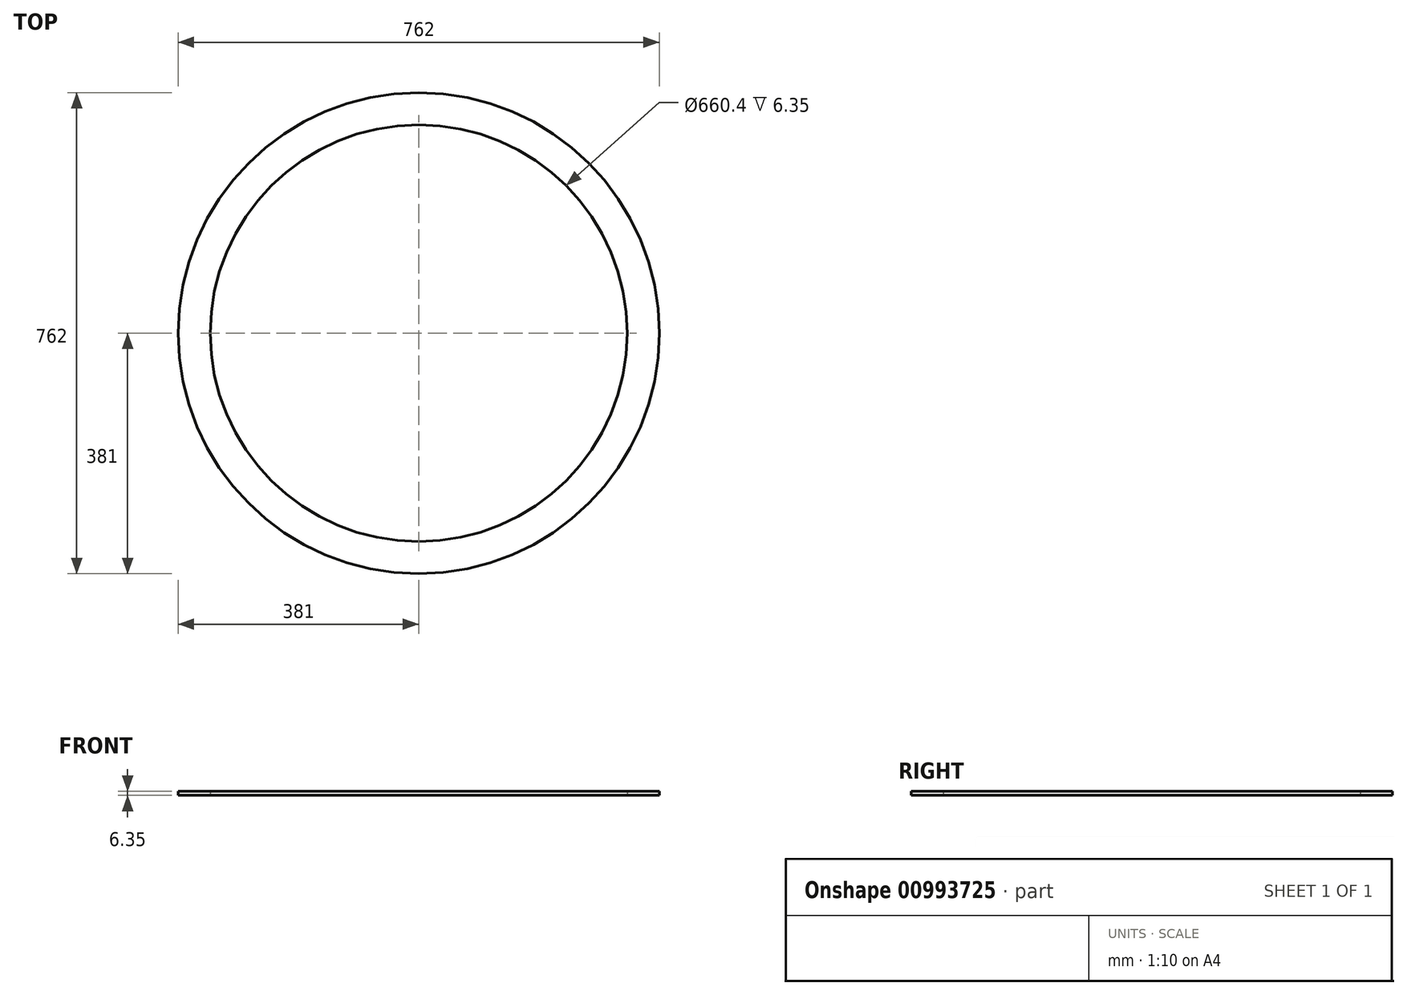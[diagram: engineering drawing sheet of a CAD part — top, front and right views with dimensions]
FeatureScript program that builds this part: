
annotation { "Feature Type Name" : "Feature", "Feature Type Description" : "" }
export const myFeature = defineFeature(function(context is Context, id is Id, definition is map)
    precondition{}
    {
        {
            var Q0;
            Q0=qCreatedBy(makeId("Top.planeOp"),FACE);
            var sketch = newSketch(context, id + "F0", { "sketchPlane" : qUnion([Q0])});
            skCircle(sketch, "E0", {"center": v(0, 0) * mm, "radius": 381 * mm});
            skCircle(sketch, "E1", {"center": v(0, 0) * mm, "radius": 330.2 * mm});
            skSolve(sketch);
        }
        {
            var Q0;
            Q0=makeQuery(id+"F0.imprint","IMPRINT",FACE,{"disambiguationData":[TD([[makeQuery(id+"F0.imprint","IMPRINT",EDGE,{"derivedFrom":sQuery(id+"F0.wireOp",EDGE,"E0")}),1.0]])]});
            extrude(context, id + "F1", {"entities" : qUnion([Q0]), "depth" : 6.35 * mm, "offsetDistance" : 25.4 * mm});
        }
    });
